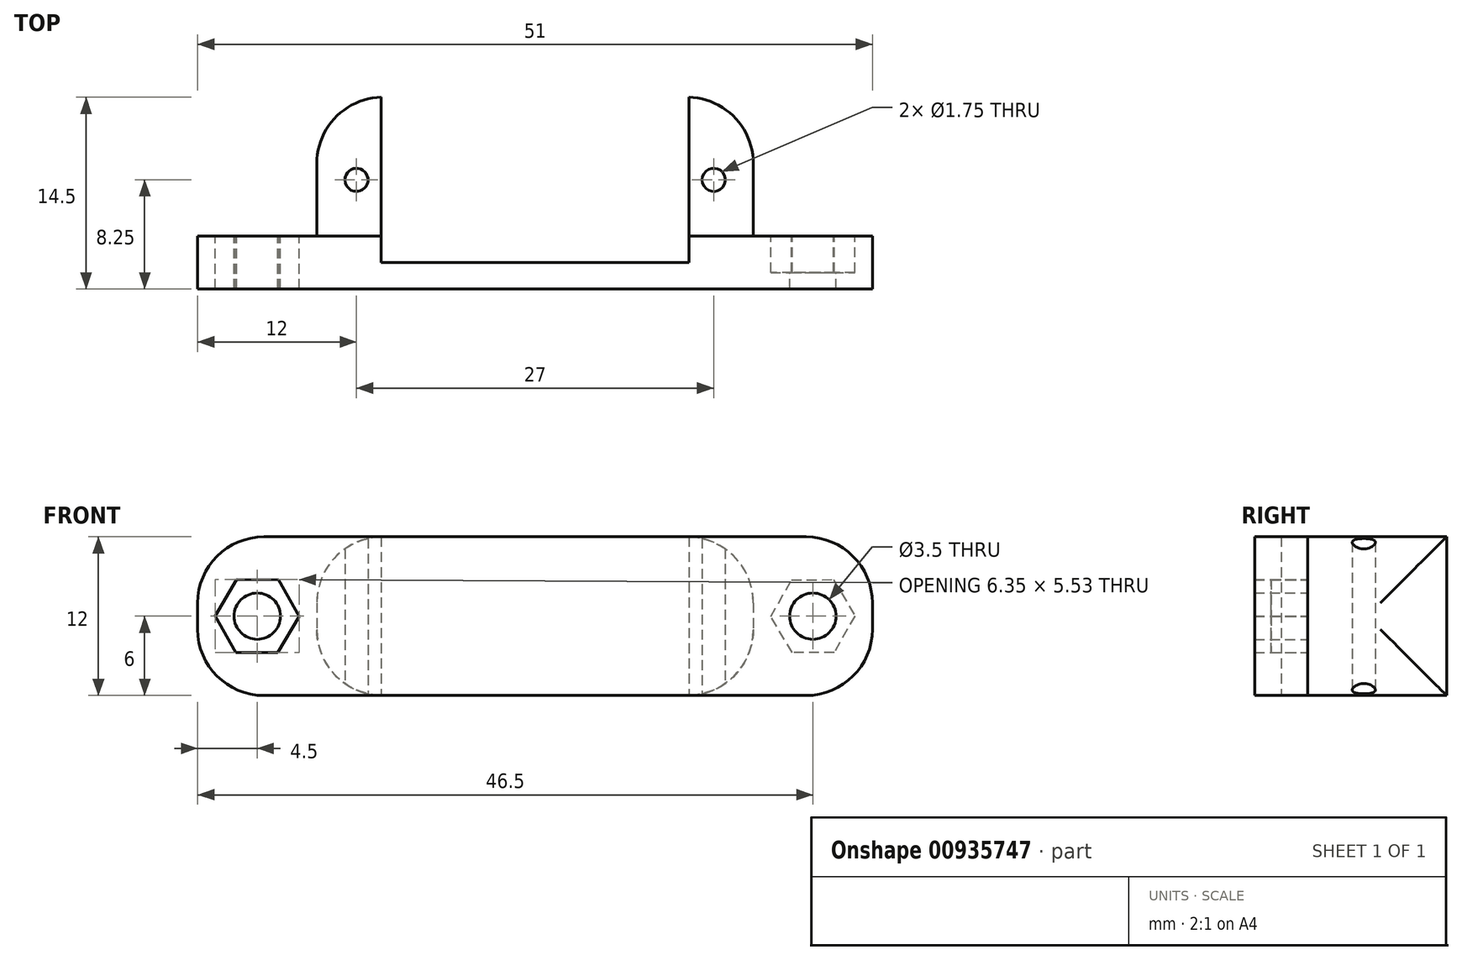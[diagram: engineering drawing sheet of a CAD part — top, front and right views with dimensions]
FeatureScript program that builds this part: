
annotation { "Feature Type Name" : "Feature", "Feature Type Description" : "" }
export const myFeature = defineFeature(function(context is Context, id is Id, definition is map)
    precondition{}
    {
        {
            var Q0;
            Q0=qCreatedBy(makeId("Top.planeOp"),FACE);
            var sketch = newSketch(context, id + "F0", { "sketchPlane" : qUnion([Q0])});
            skLineSegment(sketch, "E0.bottom", {"start": v(16.5, 7.25) * mm, "end": v(-16.5, 7.25) * mm});
            skLineSegment(sketch, "E0.top", {"start": v(16.5, -7.25) * mm, "end": v(-16.5, -7.25) * mm});
            skLineSegment(sketch, "E0.left", {"start": v(16.5, 7.25) * mm, "end": v(16.5, -7.25) * mm});
            skLineSegment(sketch, "E0.right", {"start": v(-16.5, 7.25) * mm, "end": v(-16.5, -7.25) * mm});
            skPoint(sketch, "E0.middle", {"position": v(0, 0) * mm});
            skLineSegment(sketch, "E1", {"start": v(-16.5, -5.25) * mm, "end": v(16.5, -5.25) * mm});
            skLineSegment(sketch, "E2", {"start": v(-11.63, 7.25) * mm, "end": v(-11.63, -5.25) * mm});
            skLineSegment(sketch, "E3.MirrorCS", {"start": v(11.63, 7.25) * mm, "end": v(11.63, -5.25) * mm});
            skCircle(sketch, "E4", {"center": v(-13.5, 1) * mm, "radius": 0.88 * mm});
            skLineSegment(sketch, "E5.bottom", {"start": v(-16.5, -7.25) * mm, "end": v(-25.5, -7.25) * mm});
            skLineSegment(sketch, "E5.top", {"start": v(-16.5, -3.25) * mm, "end": v(-25.5, -3.25) * mm});
            skLineSegment(sketch, "E5.left", {"start": v(-16.5, -7.25) * mm, "end": v(-16.5, -3.25) * mm});
            skLineSegment(sketch, "E5.right", {"start": v(-25.5, -7.25) * mm, "end": v(-25.5, -3.25) * mm});
            skLineSegment(sketch, "E6.MirrorCS", {"start": v(16.5, -3.25) * mm, "end": v(25.5, -3.25) * mm});
            skLineSegment(sketch, "E7.MirrorCS", {"start": v(25.5, -7.25) * mm, "end": v(25.5, -3.25) * mm});
            skLineSegment(sketch, "E8.MirrorCS", {"start": v(16.5, -7.25) * mm, "end": v(25.5, -7.25) * mm});
            skCircle(sketch, "E9.MirrorC", {"center": v(13.5, 1) * mm, "radius": 0.88 * mm});
            skSolve(sketch);
        }
        {
            var Q0;
            {var subQ4=sQuery(id+"F0.wireOp",EDGE,"E0.right");Q0=makeQuery(id+"F0.imprint","IMPRINT",FACE,{"disambiguationData":[TD([[makeQuery(id+"F0.imprint","IMPRINT",EDGE,{"derivedFrom":subQ4}),1.0]])]});}
            var Q1;
            {var subQ3=sQuery(id+"F0.wireOp",EDGE,"E5.bottom");Q1=makeQuery(id+"F0.imprint","IMPRINT",FACE,{"disambiguationData":[TD([[makeQuery(id+"F0.imprint","IMPRINT",EDGE,{"derivedFrom":subQ3}),-1.0]])]});}
            var Q2;
            {var subQ6=sQuery(id+"F0.wireOp",EDGE,"E3.MirrorCS");Q2=makeQuery(id+"F0.imprint","IMPRINT",FACE,{"disambiguationData":[TD([[makeQuery(id+"F0.imprint","IMPRINT",EDGE,{"derivedFrom":subQ6}),1.0]])]});}
            var Q3;
            {var subQ0=sQuery(id+"F0.wireOp",EDGE,"E6.MirrorCS");Q3=makeQuery(id+"F0.imprint","IMPRINT",FACE,{"disambiguationData":[TD([[makeQuery(id+"F0.imprint","IMPRINT",EDGE,{"derivedFrom":subQ0}),-1.0]])]});}
            var Q4;
            {var subQ4=sQuery(id+"F0.wireOp",EDGE,"E0.top");Q4=makeQuery(id+"F0.imprint","IMPRINT",FACE,{"disambiguationData":[TD([[makeQuery(id+"F0.imprint","IMPRINT",EDGE,{"derivedFrom":subQ4}),-1.0]])]});}
            extrude(context, id + "F1", {"entities" : qUnion([Q0, Q1, Q2, Q3, Q4]), "depth" : 12 * mm, "offsetDistance" : 25 * mm});
        }
        {
            var Q0;
            Q0=qCreatedBy(makeId("Front.planeOp"),FACE);
            var sketch = newSketch(context, id + "F2", { "sketchPlane" : qUnion([Q0])});
            skCircle(sketch, "E10.cCircle", {"center": v(21, 6) * mm, "radius": 2.75 * mm, "construction": true});
            skLineSegment(sketch, "E10.0", {"start": v(19.43, 3.24) * mm, "end": v(17.82, 5.97) * mm});
            skLineSegment(sketch, "E10.1", {"start": v(17.82, 5.97) * mm, "end": v(19.39, 8.74) * mm});
            skLineSegment(sketch, "E10.2", {"start": v(19.39, 8.74) * mm, "end": v(22.57, 8.76) * mm});
            skLineSegment(sketch, "E10.3", {"start": v(22.57, 8.76) * mm, "end": v(24.18, 6.03) * mm});
            skLineSegment(sketch, "E10.4", {"start": v(24.18, 6.03) * mm, "end": v(22.61, 3.26) * mm});
            skLineSegment(sketch, "E10.5", {"start": v(22.61, 3.26) * mm, "end": v(19.43, 3.24) * mm});
            skPoint(sketch, "E10.0.midPoint", {"position": v(18.63, 4.6) * mm});
            skCircle(sketch, "E11", {"center": v(21, 6) * mm, "radius": 1.75 * mm});
            skCircle(sketch, "E12.MirrorC", {"center": v(-21, 6) * mm, "radius": 1.75 * mm});
            skCircle(sketch, "E13.MirrorC", {"center": v(-21, 6) * mm, "radius": 2.75 * mm, "construction": true});
            skLineSegment(sketch, "E14.MirrorCS", {"start": v(-19.43, 3.24) * mm, "end": v(-17.82, 5.97) * mm});
            skLineSegment(sketch, "E15.MirrorCS", {"start": v(-19.39, 8.74) * mm, "end": v(-22.57, 8.76) * mm});
            skLineSegment(sketch, "E16.MirrorCS", {"start": v(-22.61, 3.26) * mm, "end": v(-19.43, 3.24) * mm});
            skLineSegment(sketch, "E17.MirrorCS", {"start": v(-22.57, 8.76) * mm, "end": v(-24.18, 6.03) * mm});
            skLineSegment(sketch, "E18.MirrorCS", {"start": v(-24.18, 6.03) * mm, "end": v(-22.61, 3.26) * mm});
            skPoint(sketch, "E19.MirrorP", {"position": v(-18.63, 4.6) * mm});
            skLineSegment(sketch, "E20.MirrorCS", {"start": v(-17.82, 5.97) * mm, "end": v(-19.39, 8.74) * mm});
            skSolve(sketch);
        }
        {
            var Q0;
            Q0=makeQuery(id+"F2.imprint","IMPRINT",FACE,{"disambiguationData":[TD([[makeQuery(id+"F2.imprint","IMPRINT",EDGE,{"derivedFrom":sQuery(id+"F2.wireOp",EDGE,"E11")}),1.0]])]});
            var Q1;
            Q1=makeQuery(id+"F2.imprint","IMPRINT",FACE,{"disambiguationData":[TD([[makeQuery(id+"F2.imprint","IMPRINT",EDGE,{"derivedFrom":sQuery(id+"F2.wireOp",EDGE,"E12.MirrorC")}),-1.0]])]});
            extrude(context, id + "F3", {"entities" : qUnion([Q0, Q1]), "operationType" : NewBodyOperationType.REMOVE, "depth" : 25 * mm, "offsetDistance" : 25 * mm});
        }
        {
            var Q0;
            Q0=makeQuery(id+"F2.imprint","IMPRINT",FACE,{"disambiguationData":[TD([[makeQuery(id+"F2.imprint","IMPRINT",EDGE,{"derivedFrom":sQuery(id+"F2.wireOp",EDGE,"E10.0")}),-1.0]])]});
            var Q1;
            Q1=makeQuery(id+"F2.imprint","IMPRINT",FACE,{"disambiguationData":[TD([[makeQuery(id+"F2.imprint","IMPRINT",EDGE,{"derivedFrom":sQuery(id+"F2.wireOp",EDGE,"E14.MirrorCS")}),1.0]])]});
            extrude(context, id + "F4", {"entities" : qUnion([Q0, Q1]), "operationType" : NewBodyOperationType.REMOVE, "depth" : 6 * mm, "offsetDistance" : 25 * mm});
        }
        {
            var Q0;
            Q0=makeQuery(id+"F1.opExtrude","SWEPT_EDGE",EDGE,{"disambiguationData":[OSD([sQuery(id+"F0.wireOp",EDGE,"E0.bottom"),sQuery(id+"F0.wireOp",EDGE,"E0.right")])]});
            var Q1;
            Q1=makeQuery(id+"F1.opExtrude","SWEPT_EDGE",EDGE,{"disambiguationData":[OSD([sQuery(id+"F0.wireOp",EDGE,"E0.bottom"),sQuery(id+"F0.wireOp",EDGE,"E0.left")])]});
            var Q2;
            Q2=makeQuery(id+"F1.opExtrude","CAP_EDGE",EDGE,{"disambiguationData":[OSD([sQuery(id+"F0.wireOp",EDGE,"E0.left")])],"isStart":false});
            var Q3;
            Q3=makeQuery(id+"F1.opExtrude","CAP_EDGE",EDGE,{"disambiguationData":[OSD([sQuery(id+"F0.wireOp",EDGE,"E0.left")])],"isStart":true});
            var Q4;
            Q4=makeQuery(id+"F1.opExtrude","CAP_EDGE",EDGE,{"disambiguationData":[OSD([sQuery(id+"F0.wireOp",EDGE,"E0.right")])],"isStart":true});
            var Q5;
            Q5=makeQuery(id+"F1.opExtrude","CAP_EDGE",EDGE,{"disambiguationData":[OSD([sQuery(id+"F0.wireOp",EDGE,"E0.right")])],"isStart":false});
            var Q6;
            Q6=makeQuery(id+"F1.opExtrude","CAP_EDGE",EDGE,{"disambiguationData":[OSD([sQuery(id+"F0.wireOp",EDGE,"E7.MirrorCS")])],"isStart":true});
            var Q7;
            Q7=makeQuery(id+"F1.opExtrude","CAP_EDGE",EDGE,{"disambiguationData":[OSD([sQuery(id+"F0.wireOp",EDGE,"E7.MirrorCS")])],"isStart":false});
            var Q8;
            Q8=makeQuery(id+"F1.opExtrude","CAP_EDGE",EDGE,{"disambiguationData":[OSD([sQuery(id+"F0.wireOp",EDGE,"E5.right")])],"isStart":false});
            var Q9;
            Q9=makeQuery(id+"F1.opExtrude","CAP_EDGE",EDGE,{"disambiguationData":[OSD([sQuery(id+"F0.wireOp",EDGE,"E5.right")])],"isStart":true});
            fillet(context, id + "F5", {"entities" : qUnion([Q0, Q1, Q2, Q3, Q4, Q5, Q6, Q7, Q8, Q9]), "radius" : 5 * mm, "tangentPropagation" : true, "allowEdgeOverflow" : false});
        }
    });
